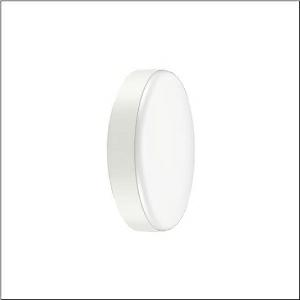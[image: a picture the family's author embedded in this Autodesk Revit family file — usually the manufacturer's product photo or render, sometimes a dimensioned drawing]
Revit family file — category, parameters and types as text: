
# Revit family: round_31_51wc10db34a
name_source: partatom
category: Lighting Fixtures
units: mm (PartAtom-declared; Revit-internal decimal feet)

## family parameters
Cut with Voids When Loaded = No
Host = Face
Light Source = No
Part Type = Normal
Room Calculation Point = No
Round Connector Dimension = Use Diameter
Shared = No

## types (1)
- Round 31 (1 x LED, 4250 lm, 34 W, 3000K)
    Apparent Load = 34 VA
    CIE Flux Codes = 44 75 94 94 100
    Color Rendering = 80
    Color Temperature = 3000K
    Default Elevation = 1800 mm
    Description = Round 31, wall and ceiling luminaire, primary optical cover: cover, of PC, opal, light emission: direct distribution, primary light characteristic: symmetric, installation type: surface-mounted, LED, rated luminous flux: 4.250lm, luminous efficacy: 125lm/W, light colour: 830, colour temperature: 3000K, control gear: DALI 2, with terminal, 5-pole, max. 2.5mm², mains connection: 220..240V, AC, 50/60Hz, rated input power: 34W, luminaire housing, of PC, traffic white (RAL 9016), diameter: 480mm, protection rating (complete): IP65, insulation class (complete): insulation class II (safety insulation), certification: CE, impact resistance: IK10, permissible operating ambient temperature: -20..+40°C, permissible storage temperature: -20..+60°C, packaging unit: 1 piece
    Height = 97 mm
    Lamp = 1 x LED
    Lamp Light Flux = 4250 lm
    Lamp Power = 34 W
    Lamp count = 1
    Length = 480 mm
    Luminous efficacy = 125 lm/W
    Manufacturer = Siteco
    ModVariant = No
    Model = 51WC10DB34A
    Mounting Place = Ceiling
    Mounting Type = Surface mounted
    Number of Poles = 1
    OnlyDefault = Yes
    Power Factor = 1
    Product Name = Round 31
    Product group = wall and ceiling luminaire | ceiling mounted
    ProductGroupID = 305
    Protection Class = Protection class II
    Protection Degree = IP 65
    RLX_Detail_Level = 1
    RLX_Emergency_Light_Flux = 0 lm
    RLX_Emergency_Type = 0
    RLX_Emergency_Type_DB = No
    RlxData = <blob elided: 41733 chars, md5=4fe240f0>
    Socket = socket
    Standby Power = 0 W
    System Light Flux = 4250 lm
    System Power = 34 W
    Type Comments = Product without accessories
    Type Image = l_1007188.jpg
    URL = http://relux.com
    VarID = ---
    Voltage = 0 V
    Weight = 0.00 kg
    Width = 0 mm  [stored 0 ft]

note: [stored X ft] marks values corroborated as IEEE doubles in the binary element streams (Revit-internal decimal feet)

## geometry (parser evidence)
native form markers: Blend x4, Sweep x11
no freeform markers — native parametric forms only
